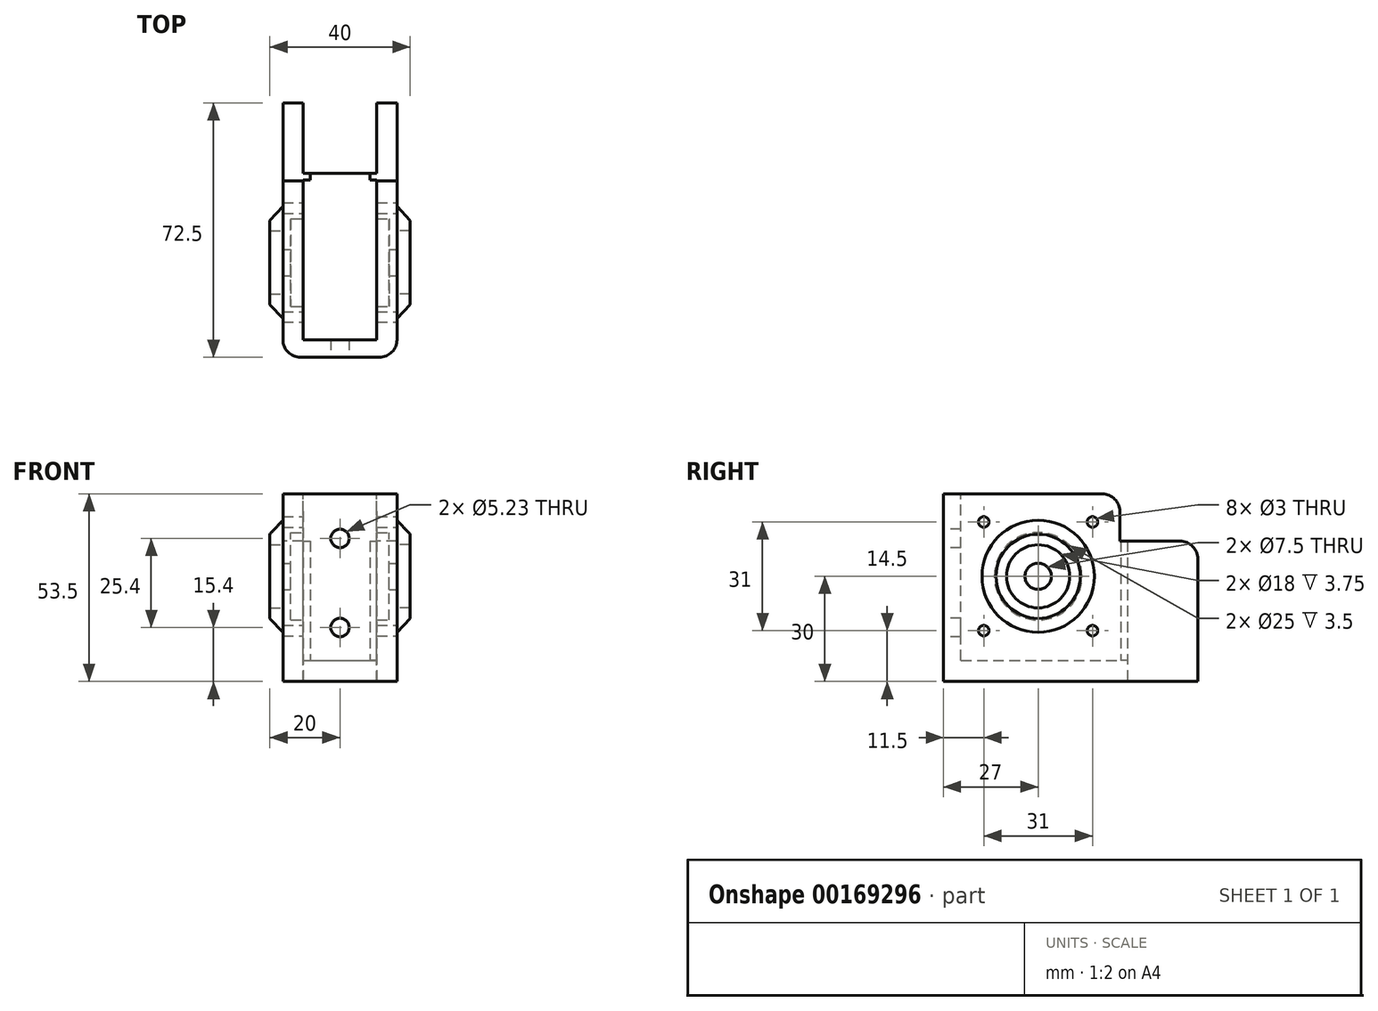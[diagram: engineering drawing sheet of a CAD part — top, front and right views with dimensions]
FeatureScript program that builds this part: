
annotation { "Feature Type Name" : "Feature", "Feature Type Description" : "" }
export const myFeature = defineFeature(function(context is Context, id is Id, definition is map)
    precondition{}
    {
        {
            var Q0;
            Q0=qCreatedBy(makeId("Right.planeOp"),FACE);
            var sketch = newSketch(context, id + "F0", { "sketchPlane" : qUnion([Q0])});
            skLineSegment(sketch, "E0.bottom", {"start": v(0, 0) * mm, "end": v(72.5, 0) * mm});
            skLineSegment(sketch, "E0.top", {"start": v(0, 53.5) * mm, "end": v(45.3, 53.5) * mm});
            skLineSegment(sketch, "E0.left", {"start": v(0, 0) * mm, "end": v(0, 53.5) * mm});
            skLineSegment(sketch, "E0.right", {"start": v(72.5, 0) * mm, "end": v(72.5, 35) * mm});
            skLineSegment(sketch, "E1", {"start": v(50.3, 48.5) * mm, "end": v(50.3, 40) * mm});
            skLineSegment(sketch, "E2", {"start": v(50.3, 40) * mm, "end": v(67.5, 40) * mm});
            skPoint(sketch, "E3.visualSharp", {"position": v(50.3, 53.5) * mm});
            skArc(sketch, "E3.filletArc", {"start": v(50.3, 48.5) * mm, "mid": v(48.84, 52.04) * mm, "end": v(45.3, 53.5) * mm});
            skPoint(sketch, "E4.visualSharp", {"position": v(72.5, 40) * mm});
            skArc(sketch, "E4.filletArc", {"start": v(72.5, 35) * mm, "mid": v(71.04, 38.54) * mm, "end": v(67.5, 40) * mm});
            skSolve(sketch);
        }
        {
            var Q0;
            Q0=makeQuery(id+"F0.imprint","IMPRINT",FACE,{"disambiguationData":[TD([[makeQuery(id+"F0.imprint","IMPRINT",EDGE,{"derivedFrom":sQuery(id+"F0.wireOp",EDGE,"E0.bottom")}),1.0]])]});
            extrude(context, id + "F1", {"entities" : qUnion([Q0]), "depth" : 32.5 * mm, "symmetric" : true});
        }
        {
            var Q0;
            Q0=qCreatedBy(makeId("Right.planeOp"),FACE);
            var sketch = newSketch(context, id + "F2", { "sketchPlane" : qUnion([Q0])});
            skCircle(sketch, "E5", {"center": v(27, 30) * mm, "radius": 3.75 * mm});
            skSolve(sketch);
        }
        {
            var Q0;
            Q0 = qSketchRegion(id + "F2", true);
            extrude(context, id + "F3", {"entities" : qUnion([Q0]), "operationType" : NewBodyOperationType.REMOVE, "endBound" : BoundingType.THROUGH_ALL, "oppositeDirection" : true, "depth" : 25 * mm, "hasSecondDirection" : true, "secondDirectionBound" : BoundingType.THROUGH_ALL, "secondDirectionOppositeDirection" : false, "secondDirectionDepth" : 25 * mm});
        }
        {
            var Q0;
            Q0=makeQuery(id+"F1.opExtrude","SWEPT_FACE",FACE,{"disambiguationData":[OSD([sQuery(id+"F0.wireOp",EDGE,"E0.top")])]});
            var sketch = newSketch(context, id + "F4", { "sketchPlane" : qUnion([Q0])});
            skLineSegment(sketch, "E6.bottom", {"start": v(-10.5, 5) * mm, "end": v(10.5, 5) * mm});
            skLineSegment(sketch, "E6.top", {"start": v(-10.5, 72.5) * mm, "end": v(10.5, 72.5) * mm});
            skLineSegment(sketch, "E6.left", {"start": v(-10.5, 5) * mm, "end": v(-10.5, 72.5) * mm});
            skLineSegment(sketch, "E6.right", {"start": v(10.5, 5) * mm, "end": v(10.5, 72.5) * mm});
            skSolve(sketch);
        }
        {
            var Q0;
            Q0 = qSketchRegion(id + "F4", true);
            extrude(context, id + "F5", {"entities" : qUnion([Q0]), "operationType" : NewBodyOperationType.REMOVE, "oppositeDirection" : true, "depth" : 47.5 * mm});
        }
        {
            var Q0;
            Q0=qCreatedBy(makeId("Front.planeOp"),FACE);
            cPlane(context, id + "F6", {"entities" : qUnion([Q0]), "cplaneType" : CPlaneType.OFFSET, "offset" : 27 * mm, "oppositeDirection" : true, "width" : 150 * mm, "height" : 150 * mm});
        }
        {
            var Q0;
            Q0=qCreatedBy(id+"F6.planeOp",FACE);
            var sketch = newSketch(context, id + "F7", { "sketchPlane" : qUnion([Q0])});
            skLineSegment(sketch, "E7", {"start": v(16.25, 46) * mm, "end": v(20, 42) * mm});
            skLineSegment(sketch, "E8", {"start": v(20, 42) * mm, "end": v(20, 39) * mm});
            skLineSegment(sketch, "E9", {"start": v(20, 39) * mm, "end": v(16.25, 39) * mm});
            skLineSegment(sketch, "E10", {"start": v(16.25, 39) * mm, "end": v(16.25, 46) * mm});
            skSolve(sketch);
        }
        {
            var Q0;
            Q0 = qSketchRegion(id + "F7", true);
            var Q1;
            Q1=makeQuery(id+"F3.boolean.opBoolean","INTERSECT",EDGE,{"derivedFrom":[makeQuery(id+"F1.opExtrude","CAP_FACE",FACE,{"disambiguationData":[OSD([sQuery(id+"F0.wireOp",EDGE,"E0.bottom"),sQuery(id+"F0.wireOp",EDGE,"E0.top"),sQuery(id+"F0.wireOp",EDGE,"E0.left"),sQuery(id+"F0.wireOp",EDGE,"E0.right"),sQuery(id+"F0.wireOp",EDGE,"E1"),sQuery(id+"F0.wireOp",EDGE,"E2"),sQuery(id+"F0.wireOp",EDGE,"E3.filletArc"),sQuery(id+"F0.wireOp",EDGE,"E4.filletArc")])],"isStart":false}),makeQuery(id+"F3.opExtrude","SWEPT_FACE",FACE,{"disambiguationData":[OSD([sQuery(id+"F2.wireOp",EDGE,"E5")])]})]});
            revolve(context, id + "F8", {"operationType" : NewBodyOperationType.ADD, "entities" : qUnion([Q0]), "axis" : qUnion([Q1]), "revolveType" : RevolveType.FULL});
        }
        {
            var Q0;
            Q0=makeQuery(id+"F1.opExtrude","SWEPT_BODY",BODY,{"disambiguationData":[OSD([sQuery(id+"F0.wireOp",EDGE,"E0.bottom"),sQuery(id+"F0.wireOp",EDGE,"E0.top"),sQuery(id+"F0.wireOp",EDGE,"E0.left"),sQuery(id+"F0.wireOp",EDGE,"E0.right"),sQuery(id+"F0.wireOp",EDGE,"E1"),sQuery(id+"F0.wireOp",EDGE,"E2"),sQuery(id+"F0.wireOp",EDGE,"E3.filletArc"),sQuery(id+"F0.wireOp",EDGE,"E4.filletArc")])]});
            var Q1;
            Q1=qCreatedBy(makeId("Right.planeOp"),FACE);
            mirror(context, id + "F9", {"operationType" : NewBodyOperationType.ADD, "entities" : qUnion([Q0]), "mirrorPlane" : qUnion([Q1])});
        }
        {
            var Q0;
            Q0=makeQuery(id+"F1.opExtrude","SWEPT_FACE",FACE,{"disambiguationData":[OSD([sQuery(id+"F0.wireOp",EDGE,"E0.right")])]});
            var sketch = newSketch(context, id + "F10", { "sketchPlane" : qUnion([Q0])});
            skLineSegment(sketch, "E11.bottom", {"start": v(-10.5, 6) * mm, "end": v(10.5, 6) * mm});
            skLineSegment(sketch, "E11.top", {"start": v(-10.5, 0) * mm, "end": v(10.5, 0) * mm});
            skLineSegment(sketch, "E11.left", {"start": v(-10.5, 6) * mm, "end": v(-10.5, 0) * mm});
            skLineSegment(sketch, "E11.right", {"start": v(10.5, 6) * mm, "end": v(10.5, 0) * mm});
            skSolve(sketch);
        }
        {
            var Q0;
            Q0 = qSketchRegion(id + "F10", true);
            extrude(context, id + "F11", {"entities" : qUnion([Q0]), "operationType" : NewBodyOperationType.REMOVE, "oppositeDirection" : true, "depth" : 20 * mm});
        }
        {
            var Q0;
            Q0=makeQuery(id+"F5.boolean.opBoolean","COPY",FACE,{"derivedFrom":makeQuery(id+"F5.opExtrude","CAP_FACE",FACE,{"disambiguationData":[OSD([sQuery(id+"F4.wireOp",EDGE,"E6.bottom"),sQuery(id+"F4.wireOp",EDGE,"E6.top"),sQuery(id+"F4.wireOp",EDGE,"E6.left"),sQuery(id+"F4.wireOp",EDGE,"E6.right")])],"isStart":false})});
            var sketch = newSketch(context, id + "F12", { "sketchPlane" : qUnion([Q0])});
            skLineSegment(sketch, "E12.bottom", {"start": v(-10.5, 52.5) * mm, "end": v(-8.5, 52.5) * mm});
            skLineSegment(sketch, "E12.top", {"start": v(-10.5, 50.5) * mm, "end": v(-8.5, 50.5) * mm});
            skLineSegment(sketch, "E12.left", {"start": v(-10.5, 52.5) * mm, "end": v(-10.5, 50.5) * mm});
            skLineSegment(sketch, "E12.right", {"start": v(-8.5, 52.5) * mm, "end": v(-8.5, 50.5) * mm});
            skLineSegment(sketch, "E13.bottom", {"start": v(10.5, 52.5) * mm, "end": v(8.5, 52.5) * mm});
            skLineSegment(sketch, "E13.top", {"start": v(10.5, 50.5) * mm, "end": v(8.5, 50.5) * mm});
            skLineSegment(sketch, "E13.left", {"start": v(10.5, 52.5) * mm, "end": v(10.5, 50.5) * mm});
            skLineSegment(sketch, "E13.right", {"start": v(8.5, 52.5) * mm, "end": v(8.5, 50.5) * mm});
            skSolve(sketch);
        }
        {
            var Q0;
            Q0 = qSketchRegion(id + "F12", true);
            var Q1;
            {var subQ1=sQuery(id+"F0.wireOp",EDGE,"E2");Q1=makeQuery(id+"F5.boolean.opBoolean","SPLIT",FACE,{"disambiguationData":[TD([makeQuery(id+"F5.opExtrude","SWEPT_FACE",FACE,{"disambiguationData":[OSD([sQuery(id+"F4.wireOp",EDGE,"E6.left")])]})])],"derivedFrom":makeQuery(id+"F1.opExtrude","SWEPT_FACE",FACE,{"disambiguationData":[OSD([subQ1])]})});}
            extrude(context, id + "F13", {"entities" : qUnion([Q0]), "operationType" : NewBodyOperationType.ADD, "endBound" : BoundingType.UP_TO_SURFACE, "endBoundEntityFace" : qUnion([Q1]), "depth" : 25 * mm});
        }
        {
            var Q0;
            Q0=qCreatedBy(makeId("Right.planeOp"),FACE);
            var sketch = newSketch(context, id + "F14", { "sketchPlane" : qUnion([Q0])});
            skCircle(sketch, "E14", {"center": v(27, 30) * mm, "radius": 12.5 * mm});
            skSolve(sketch);
        }
        {
            var Q0;
            Q0=makeQuery(id+"F14.imprint","IMPRINT",FACE,{"disambiguationData":[TD([[makeQuery(id+"F14.imprint","IMPRINT",EDGE,{"derivedFrom":sQuery(id+"F14.wireOp",EDGE,"E14")}),1.0]])]});
            extrude(context, id + "F15", {"entities" : qUnion([Q0]), "operationType" : NewBodyOperationType.REMOVE, "oppositeDirection" : true, "depth" : 28 * mm, "symmetric" : true});
        }
        {
            var Q0;
            Q0=makeQuery(id+"F1.opExtrude","CAP_EDGE",EDGE,{"disambiguationData":[OSD([sQuery(id+"F0.wireOp",EDGE,"E0.left")])],"isStart":false});
            var Q1;
            Q1=makeQuery(id+"F1.opExtrude","CAP_EDGE",EDGE,{"disambiguationData":[OSD([sQuery(id+"F0.wireOp",EDGE,"E0.left")])],"isStart":true});
            fillet(context, id + "F16", {"entities" : qUnion([Q0, Q1]), "radius" : 5 * mm, "tangentPropagation" : true, "allowEdgeOverflow" : false});
        }
        {
            var Q0;
            Q0=qCreatedBy(makeId("Right.planeOp"),FACE);
            var sketch = newSketch(context, id + "F17", { "sketchPlane" : qUnion([Q0])});
            skLineSegment(sketch, "E15.bottom", {"start": v(42.5, 14.5) * mm, "end": v(11.5, 14.5) * mm, "construction": true});
            skLineSegment(sketch, "E15.top", {"start": v(42.5, 45.5) * mm, "end": v(11.5, 45.5) * mm, "construction": true});
            skLineSegment(sketch, "E15.left", {"start": v(42.5, 14.5) * mm, "end": v(42.5, 45.5) * mm, "construction": true});
            skLineSegment(sketch, "E15.right", {"start": v(11.5, 14.5) * mm, "end": v(11.5, 45.5) * mm, "construction": true});
            skPoint(sketch, "E15.middle", {"position": v(27, 30) * mm});
            skCircle(sketch, "E16.0", {"center": v(27, 30) * mm, "radius": 3.75 * mm, "construction": true});
            skCircle(sketch, "E17", {"center": v(11.5, 45.5) * mm, "radius": 1.5 * mm});
            skCircle(sketch, "E18", {"center": v(11.5, 14.5) * mm, "radius": 1.5 * mm});
            skCircle(sketch, "E19", {"center": v(42.5, 14.5) * mm, "radius": 1.5 * mm});
            skCircle(sketch, "E20", {"center": v(42.5, 45.5) * mm, "radius": 1.5 * mm});
            skSolve(sketch);
        }
        {
            var Q0;
            Q0 = qSketchRegion(id + "F17", true);
            extrude(context, id + "F18", {"entities" : qUnion([Q0]), "operationType" : NewBodyOperationType.REMOVE, "endBound" : BoundingType.THROUGH_ALL, "oppositeDirection" : true, "depth" : 25 * mm, "hasSecondDirection" : true, "secondDirectionBound" : BoundingType.THROUGH_ALL, "secondDirectionOppositeDirection" : false, "secondDirectionDepth" : 25 * mm});
        }
        {
            var Q0;
            Q0=makeQuery(id+"F1.opExtrude","SWEPT_FACE",FACE,{"disambiguationData":[OSD([sQuery(id+"F0.wireOp",EDGE,"E0.left")])]});
            var sketch = newSketch(context, id + "F19", { "sketchPlane" : qUnion([Q0])});
            skCircle(sketch, "E21", {"center": v(0, 40.8) * mm, "radius": 2.62 * mm});
            skCircle(sketch, "E22", {"center": v(0, 15.4) * mm, "radius": 2.62 * mm});
            skSolve(sketch);
        }
        {
            var Q0;
            Q0 = qSketchRegion(id + "F19", true);
            extrude(context, id + "F20", {"entities" : qUnion([Q0]), "operationType" : NewBodyOperationType.REMOVE, "oppositeDirection" : true, "depth" : 25 * mm});
        }
    });
